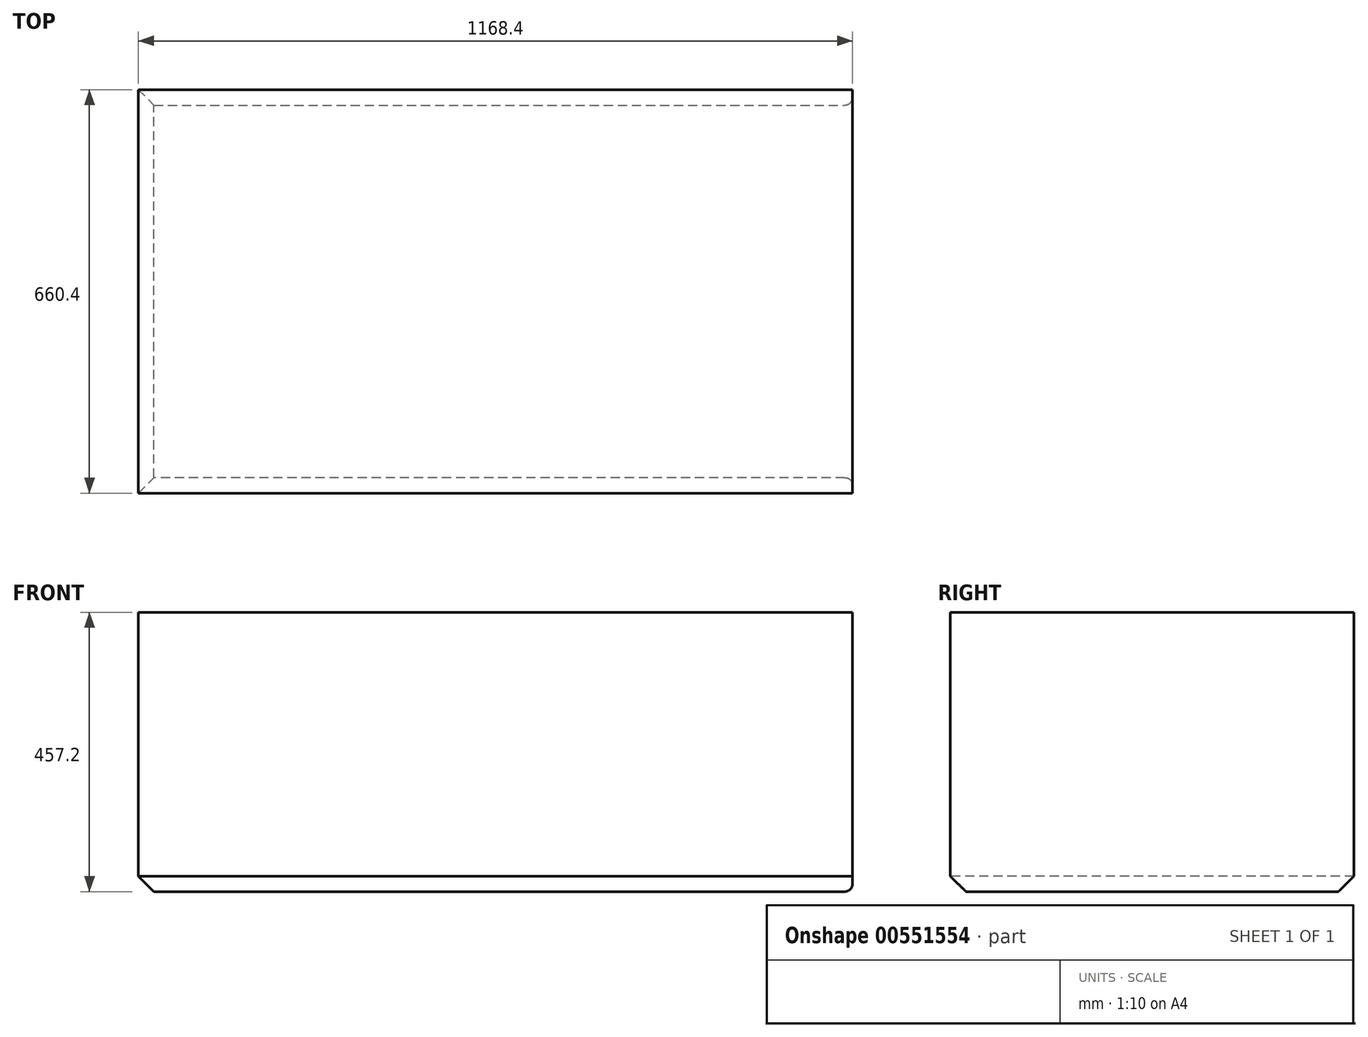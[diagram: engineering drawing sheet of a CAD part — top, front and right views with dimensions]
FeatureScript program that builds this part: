
annotation { "Feature Type Name" : "Feature", "Feature Type Description" : "" }
export const myFeature = defineFeature(function(context is Context, id is Id, definition is map)
    precondition{}
    {
        {
            var Q0;
            Q0=qCreatedBy(makeId("Front.planeOp"),FACE);
            var sketch = newSketch(context, id + "F0", { "sketchPlane" : qUnion([Q0])});
            skLineSegment(sketch, "E0.bottom", {"start": v(0, 131.88) * mm, "end": v(0, 131.88) * mm});
            skLineSegment(sketch, "E0.top", {"start": v(0, 0) * mm, "end": v(0, 0) * mm});
            skLineSegment(sketch, "E0.left", {"start": v(0, 131.88) * mm, "end": v(0, 0) * mm});
            skLineSegment(sketch, "E0.right", {"start": v(0, 131.88) * mm, "end": v(0, 0) * mm});
            skLineSegment(sketch, "E1.bottom", {"start": v(27.73, -8.7) * mm, "end": v(1196.13, -8.7) * mm});
            skLineSegment(sketch, "E1.top", {"start": v(27.73, 448.5) * mm, "end": v(1196.13, 448.5) * mm});
            skLineSegment(sketch, "E1.left", {"start": v(27.73, -8.7) * mm, "end": v(27.73, 448.5) * mm});
            skLineSegment(sketch, "E1.right", {"start": v(1196.13, -8.7) * mm, "end": v(1196.13, 448.5) * mm});
            skSolve(sketch);
        }
        {
            var Q0;
            Q0 = qSketchRegion(id + "F0", true);
            extrude(context, id + "F1", {"entities" : qUnion([Q0]), "depth" : 660.4 * mm, "offsetDistance" : 25.4 * mm});
        }
        {
            var Q0;
            Q0=makeQuery(id+"F1.opExtrude","CAP_EDGE",EDGE,{"disambiguationData":[OSD([sQuery(id+"F0.wireOp",EDGE,"E1.bottom")])],"isStart":false});
            var Q1;
            Q1=makeQuery(id+"F1.opExtrude","SWEPT_EDGE",EDGE,{"disambiguationData":[OSD([sQuery(id+"F0.wireOp",EDGE,"E1.bottom"),sQuery(id+"F0.wireOp",EDGE,"E1.left")])]});
            var Q2;
            Q2=makeQuery(id+"F1.opExtrude","CAP_EDGE",EDGE,{"disambiguationData":[OSD([sQuery(id+"F0.wireOp",EDGE,"E1.bottom")])],"isStart":true});
            chamfer(context, id + "F2", {"entities" : qUnion([Q0, Q1, Q2]), "width" : 25.4 * mm, "tangentPropagation" : true});
        }
        {
            var Q0;
            Q0=makeQuery(id+"F1.opExtrude","SWEPT_EDGE",EDGE,{"disambiguationData":[OSD([sQuery(id+"F0.wireOp",EDGE,"E1.bottom"),sQuery(id+"F0.wireOp",EDGE,"E1.right")])]});
            fillet(context, id + "F3", {"entities" : qUnion([Q0]), "radius" : 12.7 * mm, "allowEdgeOverflow" : false});
        }
    });
